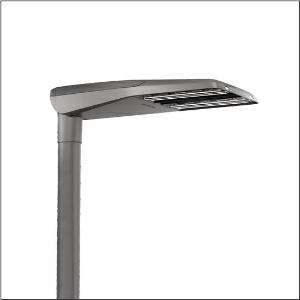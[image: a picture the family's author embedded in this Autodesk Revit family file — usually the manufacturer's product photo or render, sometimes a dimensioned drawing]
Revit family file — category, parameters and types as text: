
# Revit family: streetlight_sl_11_iq_midi___st1_0st0_5_5xc3j51g08me_56cc
name_source: partatom
category: Lighting Fixtures
units: mm (PartAtom-declared; Revit-internal decimal feet)

## family parameters
Cut with Voids When Loaded = No
Host = Face
Light Source = No
Part Type = Normal
Room Calculation Point = No
Round Connector Dimension = Use Diameter
Shared = No

## types (1)
- --- (1 x LED, 9460 lm, 63 W, 3000K)
    Apparent Load = 63 VA
    CIE Flux Codes = 35 68 96 100 100
    Color Rendering = 70
    Color Temperature = 3000K
    Default Elevation = 1800 mm
    Description = Streetlight SL 11 iQ midi, mast luminaire, primary light control with 3 zone facetted reflector, of plastic, silver coated, highly specular, primary optical cover: cover, of PMMA, transparent, light distribution: ST1.0ST0.5, light emission: direct distribution, primary light characteristic: asymmetric, installation type: post-top, side-entry, LED, High Power LED, rated luminous flux: 9.460lm, luminous efficacy: 150lm/W, light colour: 730, colour temperature: 3000K, control: Street-Remote, Auto-Match, Temp-Guard, Lumen-Switch, Night-Set, Smart-Wire, Light-Fading, Desk-Remote (wireless, voltage-free reading and setting of iQ features in the workshop via application-optimized NFC function/RFID function), optimised constant luminous flux control (CLO 2.0), presetting dimming linear, with cable H07RN-F 5x 1.5mm², mains connection: 230..240V, AC, 50/60Hz, connection cable pre-assembled, cable length: 12,5m, start of lifetime: 63W, end of service life: 67W, reduction: 30W, luminaire housing, of diecast aluminium, powder-coated, Siteco® metallic grey (DB 702S), please order mast flange separately, inclination adjustable without tools: 0°, 5°, 10°, 15° (post-top) | 0°, -5°, -10°, -15° (side-entry), sealing non-destructively replaceable, multi-level sealing system, length: 780mm, width: 376mm, height: 118mm, mast flange for spigot size: 42mm (side-entry): 5XC10008XM4, 60/48mm (side-entry/post-top): 5XC10108XM2, 76/60mm (side-entry/post-top): 5XC10108XM1, equipment: Power, protection rating (complete): IP66, insulation class (complete): insulation class II (safety insulation), certification: CE, ENEC, VDE, impact resistance: IK09, permissible operating ambient temperature for outdoor applications: -25..+50°C, standard-compliant lighting for roads and squares, Environmental Product Declaration (EPD) tested and certified by an independent institute, packaging unit: 1 piece

Light Distribution: ST1.0ST0.5
    Height = 118 mm
    Lamp = 1 x LED
    Lamp Light Flux = 9460 lm
    Lamp Power = 63 W
    Lamp count = 1
    Length = 780 mm
    Luminous efficacy = 150 lm/W
    Manufacturer = Siteco
    ModVariant = No
    Model = 5XC3J51G08ME
    Number of Poles = 1
    OnlyDefault = Yes
    Power Factor = 1
    Product Name = Streetlight SL 11 iQ midi | ST1.0ST0.5
    Product group = mast luminaire | pylon top
    ProductGroupID = 6100
    Protection Class = Protection class II
    Protection Degree = IP 66
    RLX_Detail_Level = 1
    RLX_Emergency_Light_Flux = 0 lm
    RLX_Emergency_Type = 0
    RLX_Emergency_Type_DB = No
    RlxData = <blob elided: 70641 chars, md5=570984c0>
    Socket = socket
    Standby Power = 0 W
    System Light Flux = 9460 lm
    System Power = 63 W
    Type Comments = factory setting: luminous flux: 100 % | dim-lin: 254 | 553 mA
    Type Image = l_1005960.jpg
    URL = http://relux.com
    VarID = @adj_002959
    Voltage = 0 V
    Weight = 0.00 kg
    Width = 376 mm

## geometry (parser evidence)
native form markers: Blend x4, Sweep x8
no freeform markers — native parametric forms only
